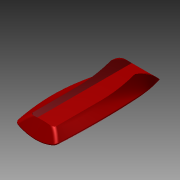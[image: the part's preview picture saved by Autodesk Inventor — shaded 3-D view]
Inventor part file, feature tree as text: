
AUTODESK INVENTOR PART (.ipt)
format: ipt  version: 2011 (Build 150239000, 239)  size: 513,024 bytes
history: native  units: mm (DEFAULTED — no unit token found)
features: other x3, plane x2, sketch x1, extrude x1, split x1, imported_body x1
ambient origin geometry x8: Origin, YZ Plane, XZ Plane, XY Plane, X Axis, Y Axis, Z Axis, Center Point
bodies: Solid1 (feature_tree)
feature tree (9):
  other  "Bottom - Master.ipt"
  sketch  "Sketch3"  dims[d1=10.0mm d9=0.0mm d10=25.4mm d15=25.4mm d16=0.0mm]
  plane  "Work Plane1"
  plane  "Work Plane2"
  extrude  "Extrusion3"  Depth=25.4mm TaperAngle=0.0deg
  split  "Split3"
  other  "Split Line"
  other  "Srf1"
  imported_body  "DerivedBody::Bottom - Master.ipt"
